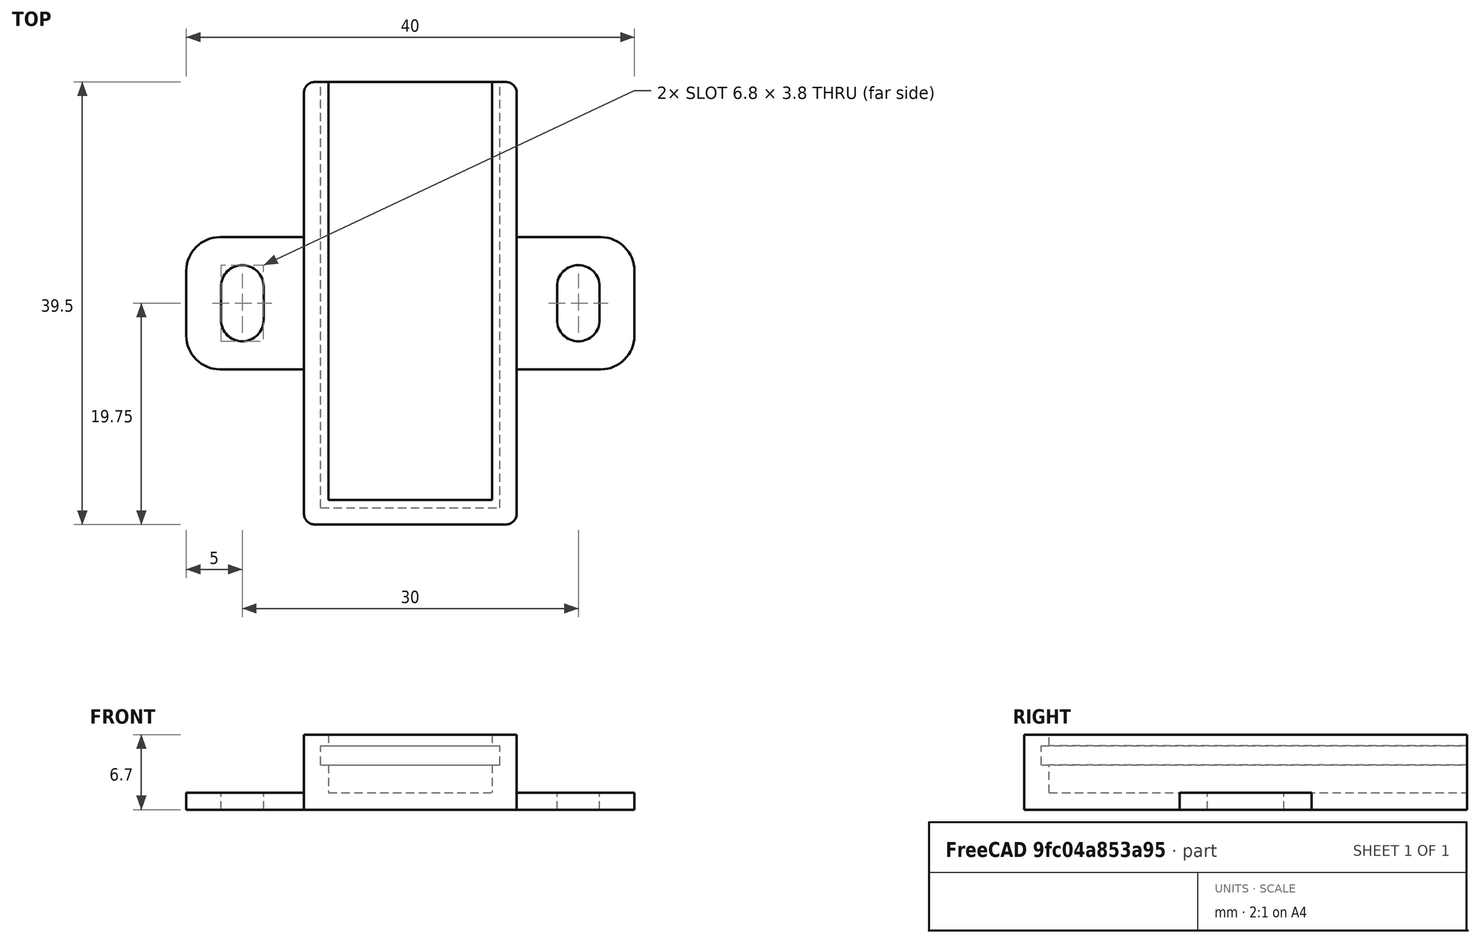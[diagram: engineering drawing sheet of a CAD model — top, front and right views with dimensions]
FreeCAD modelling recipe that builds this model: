
FCSTD DOCUMENT  (FreeCAD 0.19R23578 (Git))
Label: tp4056_usb_lion_charger
License: FreeArt
LicenseURL: http://artlibre.org/licence/lal
objects: Part::Box×3, Part::MultiFuse×2, Spreadsheet::Sheet×1, Part::Fillet×1, Part::Feature×1, Part::Cut×1, App::Part×1
note: 8 computed .brp shape members not serialized (recipe doc carries the construction recipe); baked Part::Feature solids carry a one-line shape summary decoded from their .brp

FEATURE [Spreadsheet::Sheet] Spreadsheet  label="p"
  cells = A1=pcb_x; B1(pcb_x)=16; A2=pcb_y; B2(pcb_y)=38; A3=pcb_z; B3(pcb_z)=1.7; A4=pcb_under; B4(pcb_under)=2.5; A5=side_wall; B5(side_wall)=1.5; A6=pcb_side_lane; B6(pcb_side_lane)=0.7; A7=bottom_wall; B7(bottom_wall)=1.5; A8=pcb_above; B8(pcb_above)=1
FEATURE [Part::Box] Box  label="external cube"
  AttacherType = Attacher::AttachEngine3D
  Height = 6.7
  Length = 19
  Width = 39.5
  expr: Length = <<p>>.pcb_x + 2 * <<p>>.side_wall
  expr: Width = <<p>>.pcb_y + <<p>>.side_wall
  expr: Height = <<p>>.bottom_wall + <<p>>.pcb_under + <<p>>.pcb_z + <<p>>.pcb_above
FEATURE [Part::Box] Box006  label="internal cube"
  AttacherType = Attacher::AttachEngine3D
  Height = 5.2
  Length = 14.6
  Placement = pos=(2.2,2.2,1.5) rot=(0,0,1;0rad)
  Width = 38.1
  expr: Length = <<p>>.pcb_x - 2 * <<p>>.pcb_side_lane
  expr: Width = <<p>>.pcb_y - 2 * <<p>>.pcb_side_lane + <<p>>.side_wall
  expr: Height = <<p>>.pcb_under + <<p>>.pcb_z + <<p>>.pcb_above
  expr: .Placement.Base.z = <<p>>.bottom_wall
  expr: .Placement.Base.x = <<p>>.side_wall + <<p>>.pcb_side_lane
  expr: .Placement.Base.y = <<p>>.side_wall + <<p>>.pcb_side_lane
FEATURE [Part::Box] Box007  label="pcb extract cube"
  AttacherType = Attacher::AttachEngine3D
  Height = 1.7
  Length = 16
  Placement = pos=(1.5,1.5,4) rot=(0,0,1;0rad)
  Width = 38
  expr: Height = <<p>>.pcb_z
  expr: .Placement.Base.z = <<p>>.bottom_wall + <<p>>.pcb_under
  expr: Width = <<p>>.pcb_y
  expr: Length = <<p>>.pcb_x
  expr: .Placement.Base.x = <<p>>.side_wall
  expr: .Placement.Base.y = <<p>>.side_wall
FEATURE [Part::MultiFuse] Fusion  label="extract fusion"
  Shapes = -> [Box006,Box007]
FEATURE [Part::Fillet] Fillet  label="external fillet"
  Base = -> Box
  Edges = 4 edges r=1: [Edge1,Edge3,Edge5,Edge7]
FEATURE [Part::Feature] Cut003001  label="attach plane x dir001"
  Placement = pos=(-10.5,13.85,0) rot=(0,0,1;0rad)
  shape: bbox 40 x 11.8 x 1.5 mm, 18 faces (baked)
FEATURE [Part::MultiFuse] Fusion001  label="body fusion"
  Shapes = -> [Fillet,Cut003001]
FEATURE [Part::Cut] Cut  label="body cut"
  Base = -> Fusion001
  Tool = -> Fusion
FEATURE [App::Part] Part  label="pcb box part"
  Group = -> [Box,Fillet,Fusion001,Fusion,Box007,Box006,Cut]
  Origin = -> Origin
